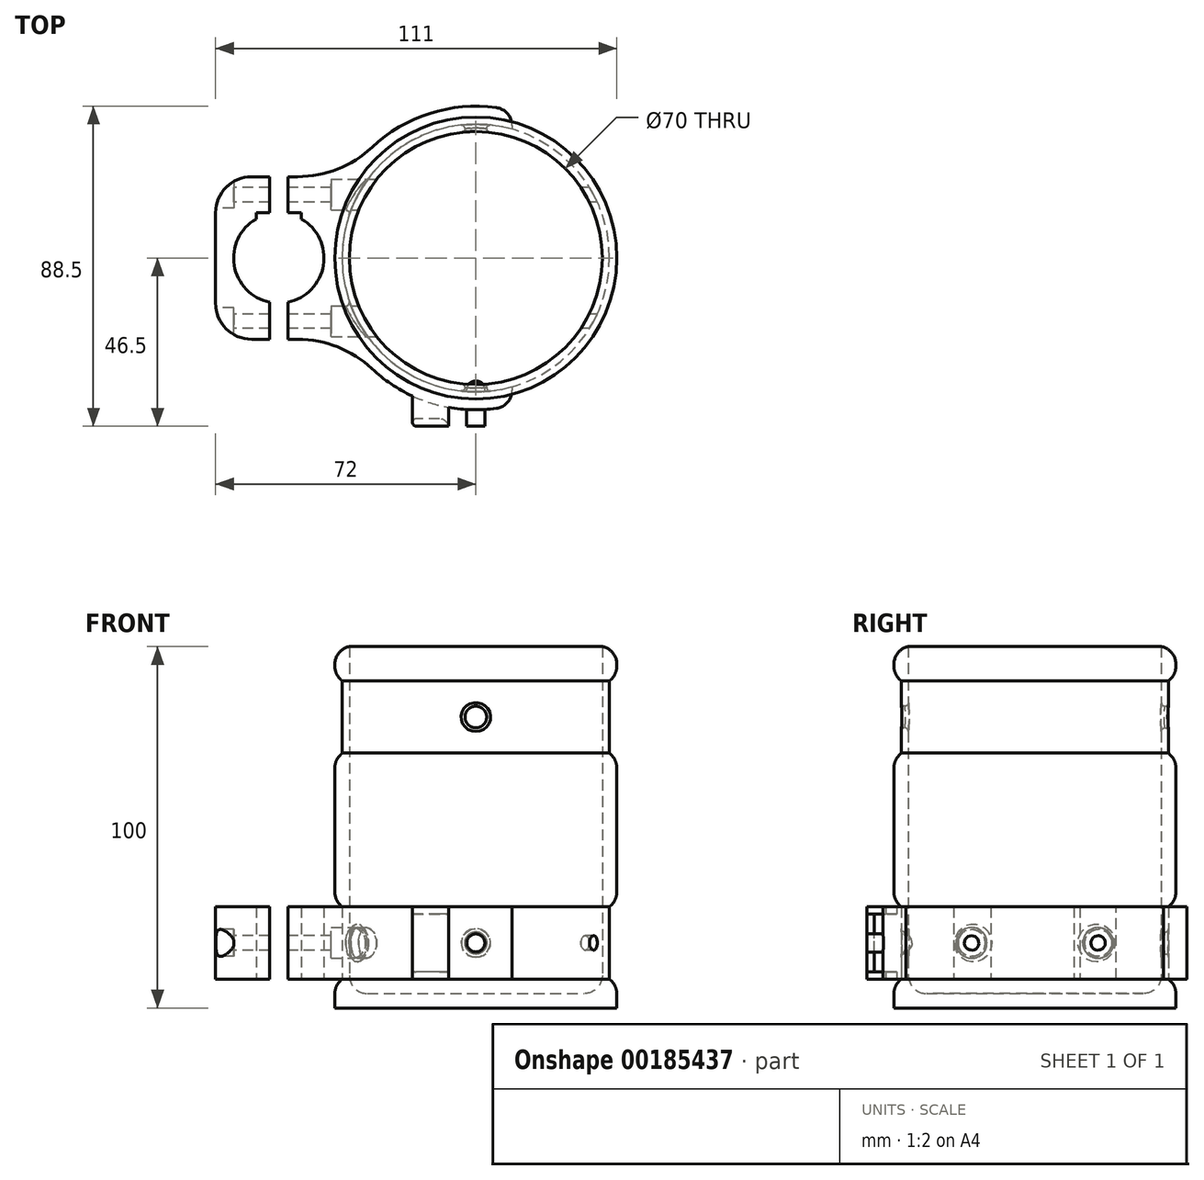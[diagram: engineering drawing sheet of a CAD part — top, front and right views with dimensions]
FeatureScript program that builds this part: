
annotation { "Feature Type Name" : "Feature", "Feature Type Description" : "" }
export const myFeature = defineFeature(function(context is Context, id is Id, definition is map)
    precondition{}
    {
        {
            var Q0;
            Q0=qCreatedBy(makeId("Front.planeOp"),FACE);
            var sketch = newSketch(context, id + "F0", { "sketchPlane" : qUnion([Q0])});
            skLineSegment(sketch, "E0", {"start": v(0, 0) * mm, "end": v(35, 0) * mm});
            skLineSegment(sketch, "E1", {"start": v(35, 0) * mm, "end": v(35, 100) * mm});
            skLineSegment(sketch, "E2", {"start": v(35, 100) * mm, "end": v(39, 100) * mm});
            skLineSegment(sketch, "E3", {"start": v(39, 100) * mm, "end": v(39, 92.5) * mm});
            skLineSegment(sketch, "E4", {"start": v(39, 92.5) * mm, "end": v(37, 90.5) * mm});
            skLineSegment(sketch, "E5", {"start": v(37, 90.5) * mm, "end": v(37, 70.5) * mm});
            skLineSegment(sketch, "E6", {"start": v(37, 70.5) * mm, "end": v(39, 68.5) * mm});
            skLineSegment(sketch, "E7", {"start": v(39, 68.5) * mm, "end": v(39, 30) * mm});
            skLineSegment(sketch, "E8", {"start": v(39, 30) * mm, "end": v(37, 28) * mm});
            skLineSegment(sketch, "E9", {"start": v(37, 28) * mm, "end": v(37, 8) * mm});
            skLineSegment(sketch, "E10", {"start": v(37, 8) * mm, "end": v(39, 6) * mm});
            skLineSegment(sketch, "E11", {"start": v(39, 6) * mm, "end": v(39, 0) * mm});
            skLineSegment(sketch, "E12", {"start": v(39, 0) * mm, "end": v(35, 0) * mm});
            skLineSegment(sketch, "E13", {"start": v(37, 8) * mm, "end": v(37, 6) * mm, "construction": true});
            skLineSegment(sketch, "E14", {"start": v(37, 6) * mm, "end": v(39, 6) * mm, "construction": true});
            skLineSegment(sketch, "E15", {"start": v(39, 30) * mm, "end": v(37, 30) * mm, "construction": true});
            skLineSegment(sketch, "E16", {"start": v(37, 30) * mm, "end": v(37, 28) * mm, "construction": true});
            skLineSegment(sketch, "E17", {"start": v(37, 70.5) * mm, "end": v(37, 68.5) * mm, "construction": true});
            skLineSegment(sketch, "E18", {"start": v(37, 68.5) * mm, "end": v(39, 68.5) * mm, "construction": true});
            skLineSegment(sketch, "E19", {"start": v(39, 92.5) * mm, "end": v(37, 92.5) * mm, "construction": true});
            skLineSegment(sketch, "E20", {"start": v(37, 92.5) * mm, "end": v(37, 90.5) * mm, "construction": true});
            skLineSegment(sketch, "E21", {"start": v(37, 6) * mm, "end": v(35, 6) * mm, "construction": true});
            skLineSegment(sketch, "E22", {"start": v(0, 0) * mm, "end": v(0, 100) * mm, "construction": true});
            skLineSegment(sketch, "E23", {"start": v(0, 100) * mm, "end": v(35, 100) * mm, "construction": true});
            skLineSegment(sketch, "E24", {"start": v(0, 4) * mm, "end": v(35, 4) * mm});
            skLineSegment(sketch, "E25", {"start": v(0, 4) * mm, "end": v(0, 0) * mm});
            skSolve(sketch);
        }
        {
            var Q0;
            Q0 = qSketchRegion(id + "F0", true);
            var Q1;
            Q1=sQuery(id+"F0.wireOp",EDGE,"E22");
            revolve(context, id + "F1", {"surfaceOperationType" : NewSurfaceOperationType.NEW, "entities" : qUnion([Q0]), "axis" : qUnion([Q1]), "revolveType" : RevolveType.FULL});
        }
        {
            var Q0;
            Q0=qCreatedBy(makeId("Front.planeOp"),FACE);
            var sketch = newSketch(context, id + "F2", { "sketchPlane" : qUnion([Q0])});
            skPoint(sketch, "E26", {"position": v(0, 28) * mm});
            skPoint(sketch, "E27", {"position": v(0, 8) * mm});
            skPoint(sketch, "E28", {"position": v(0, 70.5) * mm});
            skPoint(sketch, "E29", {"position": v(0, 90.5) * mm});
            skLineSegment(sketch, "E30", {"start": v(0, 70.5) * mm, "end": v(0, 90.5) * mm, "construction": true});
            skLineSegment(sketch, "E31", {"start": v(0, 8) * mm, "end": v(0, 28) * mm, "construction": true});
            skPoint(sketch, "E32", {"position": v(0, 18) * mm});
            skPoint(sketch, "E33", {"position": v(0, 80.5) * mm});
            skCircle(sketch, "E34", {"center": v(0, 18) * mm, "radius": 3 * mm});
            skCircle(sketch, "E35", {"center": v(0, 80.5) * mm, "radius": 3 * mm});
            skSolve(sketch);
        }
        {
            var Q0;
            Q0 = qSketchRegion(id + "F2", true);
            extrude(context, id + "F3", {"entities" : qUnion([Q0]), "operationType" : NewBodyOperationType.REMOVE, "oppositeDirection" : true, "depth" : 80 * mm, "symmetric" : true});
        }
        {
            var Q0;
            Q0=makeQuery(id+"F3.boolean.opBoolean","INTERSECT",EDGE,{"disambiguationData":[OD(0.0)],"derivedFrom":[makeQuery(id+"F1.opRevolve","SWEPT_FACE",FACE,{"disambiguationData":[OSD([sQuery(id+"F0.wireOp",EDGE,"E1")])]}),makeQuery(id+"F3.opExtrude","SWEPT_FACE",FACE,{"disambiguationData":[OSD([sQuery(id+"F2.wireOp",EDGE,"E35")])]})]});
            var Q1;
            Q1=makeQuery(id+"F3.boolean.opBoolean","INTERSECT",EDGE,{"disambiguationData":[OD(0.0)],"derivedFrom":[makeQuery(id+"F1.opRevolve","SWEPT_FACE",FACE,{"disambiguationData":[OSD([sQuery(id+"F0.wireOp",EDGE,"E5")])]}),makeQuery(id+"F3.opExtrude","SWEPT_FACE",FACE,{"disambiguationData":[OSD([sQuery(id+"F2.wireOp",EDGE,"E35")])]})]});
            var Q2;
            Q2=makeQuery(id+"F3.boolean.opBoolean","INTERSECT",EDGE,{"disambiguationData":[OD(0.0)],"derivedFrom":[makeQuery(id+"F1.opRevolve","SWEPT_FACE",FACE,{"disambiguationData":[OSD([sQuery(id+"F0.wireOp",EDGE,"E1")])]}),makeQuery(id+"F3.opExtrude","SWEPT_FACE",FACE,{"disambiguationData":[OSD([sQuery(id+"F2.wireOp",EDGE,"E34")])]})]});
            var Q3;
            Q3=makeQuery(id+"F3.boolean.opBoolean","INTERSECT",EDGE,{"disambiguationData":[OD(0.0)],"derivedFrom":[makeQuery(id+"F1.opRevolve","SWEPT_FACE",FACE,{"disambiguationData":[OSD([sQuery(id+"F0.wireOp",EDGE,"E9")])]}),makeQuery(id+"F3.opExtrude","SWEPT_FACE",FACE,{"disambiguationData":[OSD([sQuery(id+"F2.wireOp",EDGE,"E34")])]})]});
            var Q4;
            Q4=makeQuery(id+"F3.boolean.opBoolean","INTERSECT",EDGE,{"disambiguationData":[OD(1.0)],"derivedFrom":[makeQuery(id+"F1.opRevolve","SWEPT_FACE",FACE,{"disambiguationData":[OSD([sQuery(id+"F0.wireOp",EDGE,"E1")])]}),makeQuery(id+"F3.opExtrude","SWEPT_FACE",FACE,{"disambiguationData":[OSD([sQuery(id+"F2.wireOp",EDGE,"E35")])]})]});
            var Q5;
            Q5=makeQuery(id+"F3.boolean.opBoolean","INTERSECT",EDGE,{"disambiguationData":[OD(1.0)],"derivedFrom":[makeQuery(id+"F1.opRevolve","SWEPT_FACE",FACE,{"disambiguationData":[OSD([sQuery(id+"F0.wireOp",EDGE,"E5")])]}),makeQuery(id+"F3.opExtrude","SWEPT_FACE",FACE,{"disambiguationData":[OSD([sQuery(id+"F2.wireOp",EDGE,"E35")])]})]});
            var Q6;
            Q6=makeQuery(id+"F3.boolean.opBoolean","INTERSECT",EDGE,{"disambiguationData":[OD(1.0)],"derivedFrom":[makeQuery(id+"F1.opRevolve","SWEPT_FACE",FACE,{"disambiguationData":[OSD([sQuery(id+"F0.wireOp",EDGE,"E1")])]}),makeQuery(id+"F3.opExtrude","SWEPT_FACE",FACE,{"disambiguationData":[OSD([sQuery(id+"F2.wireOp",EDGE,"E34")])]})]});
            var Q7;
            Q7=makeQuery(id+"F3.boolean.opBoolean","INTERSECT",EDGE,{"disambiguationData":[OD(1.0)],"derivedFrom":[makeQuery(id+"F1.opRevolve","SWEPT_FACE",FACE,{"disambiguationData":[OSD([sQuery(id+"F0.wireOp",EDGE,"E9")])]}),makeQuery(id+"F3.opExtrude","SWEPT_FACE",FACE,{"disambiguationData":[OSD([sQuery(id+"F2.wireOp",EDGE,"E34")])]})]});
            fillet(context, id + "F4", {"entities" : qUnion([Q0, Q1, Q2, Q3, Q4, Q5, Q6, Q7]), "radius" : 1 * mm, "tangentPropagation" : true, "allowEdgeOverflow" : false});
        }
        {
            var Q0;
            Q0=makeQuery(id+"F1.opRevolve","SWEPT_EDGE",EDGE,{"disambiguationData":[OSD([sQuery(id+"F0.wireOp",EDGE,"E7"),sQuery(id+"F0.wireOp",EDGE,"E8")])]});
            var Q1;
            Q1=makeQuery(id+"F1.opRevolve","SWEPT_EDGE",EDGE,{"disambiguationData":[OSD([sQuery(id+"F0.wireOp",EDGE,"E10"),sQuery(id+"F0.wireOp",EDGE,"E11")])]});
            var Q2;
            Q2=makeQuery(id+"F1.opRevolve","SWEPT_EDGE",EDGE,{"disambiguationData":[OSD([sQuery(id+"F0.wireOp",EDGE,"E6"),sQuery(id+"F0.wireOp",EDGE,"E7")])]});
            var Q3;
            Q3=makeQuery(id+"F1.opRevolve","SWEPT_EDGE",EDGE,{"disambiguationData":[OSD([sQuery(id+"F0.wireOp",EDGE,"E3"),sQuery(id+"F0.wireOp",EDGE,"E4")])]});
            var Q4;
            Q4=makeQuery(id+"F1.opRevolve","SWEPT_EDGE",EDGE,{"disambiguationData":[OSD([sQuery(id+"F0.wireOp",EDGE,"E2"),sQuery(id+"F0.wireOp",EDGE,"E3")])]});
            fillet(context, id + "F5", {"entities" : qUnion([Q0, Q1, Q2, Q3, Q4]), "radius" : 5 * mm, "tangentPropagation" : true, "allowEdgeOverflow" : false});
        }
        {
            var Q0;
            Q0=makeQuery(id+"F1.opRevolve","SWEPT_EDGE",EDGE,{"disambiguationData":[OSD([sQuery(id+"F0.wireOp",EDGE,"E1"),sQuery(id+"F0.wireOp",EDGE,"E2")])]});
            var Q1;
            Q1=makeQuery(id+"F1.opRevolve","SWEPT_EDGE",EDGE,{"disambiguationData":[OSD([sQuery(id+"F0.wireOp",EDGE,"E1"),sQuery(id+"F0.wireOp",EDGE,"E24")])]});
            fillet(context, id + "F6", {"entities" : qUnion([Q0, Q1]), "radius" : 5 * mm, "tangentPropagation" : true, "allowEdgeOverflow" : false});
        }
        {
            var Q0;
            Q0=qCreatedBy(makeId("Top.planeOp"),FACE);
            var Q1;
            Q1=sQuery(id+"F2.wireOp",VERTEX,"E32");
            cPlane(context, id + "F7", {"entities" : qUnion([Q0, Q1]), "cplaneType" : CPlaneType.PLANE_POINT, "offset" : 25 * mm, "width" : 150 * mm, "height" : 150 * mm});
        }
        {
            var Q0;
            Q0=qCreatedBy(id+"F7.planeOp",FACE);
            var sketch = newSketch(context, id + "F8", { "sketchPlane" : qUnion([Q0])});
            skLineSegment(sketch, "E36", {"start": v(2.5, 0) * mm, "end": v(-2.5, 0) * mm, "construction": true});
            skLineSegment(sketch, "E37", {"start": v(-2.5, 0) * mm, "end": v(-2.5, 37) * mm, "construction": true});
            skLineSegment(sketch, "E38", {"start": v(-2.5, 37) * mm, "end": v(2.5, 37) * mm, "construction": true});
            skLineSegment(sketch, "E39", {"start": v(2.5, 37) * mm, "end": v(2.5, 0) * mm, "construction": true});
            skLineSegment(sketch, "E40", {"start": v(-2.5, 0) * mm, "end": v(-2.5, -37) * mm, "construction": true});
            skLineSegment(sketch, "E41", {"start": v(-2.5, -37) * mm, "end": v(2.5, -37) * mm, "construction": true});
            skLineSegment(sketch, "E42", {"start": v(2.5, -37) * mm, "end": v(2.5, 0) * mm, "construction": true});
            skLineSegment(sketch, "E43", {"start": v(0, 0) * mm, "end": v(-42, 0) * mm, "construction": true});
            skArc(sketch, "E44", {"start": v(-60.75, 10.83) * mm, "mid": v(-54.5, -12.5) * mm, "end": v(-48.25, 10.83) * mm});
            skLineSegment(sketch, "E45", {"start": v(-54.5, 0) * mm, "end": v(-42, 0) * mm, "construction": true});
            skPoint(sketch, "E46", {"position": v(-48.25, 0) * mm});
            skLineSegment(sketch, "E47", {"start": v(-48.25, 10.83) * mm, "end": v(-48.25, -10.83) * mm, "construction": true});
            skArc(sketch, "E48", {"start": v(10, 35.62) * mm, "mid": v(-37, 0) * mm, "end": v(10, -35.62) * mm});
            skPoint(sketch, "E49", {"position": v(0, -37) * mm});
            skLineSegment(sketch, "E50", {"start": v(0, -37) * mm, "end": v(10, -37) * mm, "construction": true});
            skPoint(sketch, "E51", {"position": v(0, 37) * mm});
            skLineSegment(sketch, "E52", {"start": v(0, 37) * mm, "end": v(10, 37) * mm, "construction": true});
            skLineSegment(sketch, "E53", {"start": v(10, 37) * mm, "end": v(10, -37) * mm, "construction": true});
            skPoint(sketch, "E54", {"position": v(10, -35.62) * mm});
            skPoint(sketch, "E55", {"position": v(10, 35.62) * mm});
            skArc(sketch, "E56", {"start": v(10, 40.8) * mm, "mid": v(-42, 0) * mm, "end": v(10, -40.8) * mm});
            skLineSegment(sketch, "E57", {"start": v(10, -35.62) * mm, "end": v(10, -40.8) * mm});
            skLineSegment(sketch, "E58", {"start": v(10, 40.8) * mm, "end": v(10, 35.62) * mm});
            skLineSegment(sketch, "E59", {"start": v(-42, -15) * mm, "end": v(-42, 0) * mm, "construction": true});
            skLineSegment(sketch, "E60", {"start": v(-42, 15) * mm, "end": v(-42, 0) * mm, "construction": true});
            skLineSegment(sketch, "E61", {"start": v(-48.25, 12.5) * mm, "end": v(-60.75, 12.5) * mm});
            skLineSegment(sketch, "E62", {"start": v(-48.25, 12.5) * mm, "end": v(-48.25, 10.83) * mm});
            skLineSegment(sketch, "E63", {"start": v(-60.75, 12.5) * mm, "end": v(-60.75, 10.83) * mm});
            skLineSegment(sketch, "E64", {"start": v(-54.5, 12.5) * mm, "end": v(-54.5, -12.5) * mm, "construction": true});
            skPoint(sketch, "E65", {"position": v(-54.5, 12.5) * mm});
            skPoint(sketch, "E66", {"position": v(-54.5, -12.5) * mm});
            skLineSegment(sketch, "E67", {"start": v(-52, 22.5) * mm, "end": v(-52, -22.5) * mm});
            skLineSegment(sketch, "E68", {"start": v(-57, 22.5) * mm, "end": v(-57, -22.5) * mm});
            skLineSegment(sketch, "E69", {"start": v(-52, 12.5) * mm, "end": v(-57, 12.5) * mm, "construction": true});
            skLineSegment(sketch, "E70", {"start": v(-54.5, 12.5) * mm, "end": v(-54.5, 15.5) * mm, "construction": true});
            skPoint(sketch, "E71", {"position": v(-54.5, 17.5) * mm});
            skLineSegment(sketch, "E72", {"start": v(-54.5, 19.5) * mm, "end": v(-54.5, 15.5) * mm, "construction": true});
            skLineSegment(sketch, "E73.trimOffspring", {"start": v(-54.5, 19.5) * mm, "end": v(-54.5, 22.5) * mm, "construction": true});
            skLineSegment(sketch, "E74", {"start": v(-35.46, 22.5) * mm, "end": v(-72, 22.5) * mm});
            skLineSegment(sketch, "E75", {"start": v(-67, 22.5) * mm, "end": v(-67, 19.5) * mm, "construction": true});
            skLineSegment(sketch, "E76", {"start": v(-72, -22.5) * mm, "end": v(-35.46, -22.5) * mm});
            skLineSegment(sketch, "E77", {"start": v(-72, 22.5) * mm, "end": v(-72, -22.5) * mm});
            skLineSegment(sketch, "E78", {"start": v(-31.44, 19.5) * mm, "end": v(-72, 19.5) * mm, "construction": true});
            skLineSegment(sketch, "E79", {"start": v(-33.6, 15.5) * mm, "end": v(-72, 15.5) * mm, "construction": true});
            skLineSegment(sketch, "E80", {"start": v(-72, -15.5) * mm, "end": v(-33.6, -15.5) * mm, "construction": true});
            skLineSegment(sketch, "E81", {"start": v(-72, -19.5) * mm, "end": v(-31.44, -19.5) * mm, "construction": true});
            skLineSegment(sketch, "E82", {"start": v(-67, 19.5) * mm, "end": v(-67, 15.5) * mm, "construction": true});
            skLineSegment(sketch, "E83", {"start": v(-67, 15.5) * mm, "end": v(-67, -15.5) * mm, "construction": true});
            skLineSegment(sketch, "E84", {"start": v(-67, -15.5) * mm, "end": v(-67, -19.5) * mm, "construction": true});
            skLineSegment(sketch, "E85", {"start": v(-67, -19.5) * mm, "end": v(-67, -22.5) * mm, "construction": true});
            skLineSegment(sketch, "E86", {"start": v(-72, 17.5) * mm, "end": v(-32.6, 17.5) * mm, "construction": true});
            skLineSegment(sketch, "E87", {"start": v(-72, -17.5) * mm, "end": v(-32.6, -17.5) * mm, "construction": true});
            skSolve(sketch);
        }
        {
            var Q0;
            Q0=makeQuery(id+"F8.imprint","IMPRINT",FACE,{"disambiguationData":[TD([[makeQuery(id+"F8.imprint","IMPRINT",EDGE,{"derivedFrom":sQuery(id+"F8.wireOp",EDGE,"E48")}),-1.0]])]});
            var Q1;
            {var subQ0=sQuery(id+"F8.wireOp",EDGE,"E67");var subQ1=sQuery(id+"F8.wireOp",EDGE,"E44");var subQ2=makeQuery(id+"F8.imprint","INTERSECT",VERTEX,{"derivedFrom":[subQ1,subQ0]});Q1=makeQuery(id+"F8.imprint","IMPRINT",FACE,{"disambiguationData":[TD([[makeQuery(id+"F8.imprint","IMPRINT",EDGE,{"disambiguationData":[TD([[subQ2,-1.0]])],"derivedFrom":subQ1}),-1.0]])]});}
            var Q2;
            {var subQ0=sQuery(id+"F8.wireOp",EDGE,"E62");Q2=makeQuery(id+"F8.imprint","IMPRINT",FACE,{"disambiguationData":[TD([[makeQuery(id+"F8.imprint","IMPRINT",EDGE,{"derivedFrom":subQ0}),1.0]])]});}
            extrude(context, id + "F9", {"entities" : qUnion([Q0, Q1, Q2]), "depth" : 20 * mm, "symmetric" : true});
        }
        {
            var Q0;
            {var subQ5=sQuery(id+"F8.wireOp",EDGE,"E63");Q0=makeQuery(id+"F8.imprint","IMPRINT",FACE,{"disambiguationData":[TD([[makeQuery(id+"F8.imprint","IMPRINT",EDGE,{"derivedFrom":subQ5}),-1.0]])]});}
            extrude(context, id + "F10", {"entities" : qUnion([Q0]), "depth" : 20 * mm, "symmetric" : true});
        }
        {
            var Q0;
            Q0=makeQuery(id+"F9.opExtrude","SWEPT_EDGE",EDGE,{"disambiguationData":[OSD([sQuery(id+"F8.wireOp",EDGE,"E56"),sQuery(id+"F8.wireOp",EDGE,"E76")])]});
            var Q1;
            Q1=makeQuery(id+"F9.opExtrude","SWEPT_EDGE",EDGE,{"disambiguationData":[OSD([sQuery(id+"F8.wireOp",EDGE,"E56"),sQuery(id+"F8.wireOp",EDGE,"E74")])]});
            fillet(context, id + "F11", {"entities" : qUnion([Q0, Q1]), "radius" : 30 * mm, "tangentPropagation" : true, "allowEdgeOverflow" : false});
        }
        {
            var Q0;
            Q0=makeQuery(id+"F10.opExtrude","SWEPT_FACE",FACE,{"disambiguationData":[OSD([sQuery(id+"F8.wireOp",EDGE,"E77")])]});
            var sketch = newSketch(context, id + "F12", { "sketchPlane" : qUnion([Q0])});
            skPoint(sketch, "E88", {"position": v(17.5, 18) * mm});
            skPoint(sketch, "E89", {"position": v(19.5, 18) * mm});
            skPoint(sketch, "E90", {"position": v(15.5, 18) * mm});
            skCircle(sketch, "E91", {"center": v(17.5, 18) * mm, "radius": 2 * mm});
            skPoint(sketch, "E92", {"position": v(-19.5, 18) * mm});
            skPoint(sketch, "E93", {"position": v(-17.5, 18) * mm});
            skPoint(sketch, "E94", {"position": v(-15.5, 18) * mm});
            skCircle(sketch, "E95", {"center": v(-17.5, 18) * mm, "radius": 2 * mm});
            skCircle(sketch, "E96", {"center": v(-17.5, 18) * mm, "radius": 3.75 * mm});
            skCircle(sketch, "E97", {"center": v(17.5, 18) * mm, "radius": 3.75 * mm});
            skSolve(sketch);
        }
        {
            var Q0;
            Q0=makeQuery(id+"F12.imprint","IMPRINT",FACE,{"disambiguationData":[TD([[makeQuery(id+"F12.imprint","IMPRINT",EDGE,{"derivedFrom":sQuery(id+"F12.wireOp",EDGE,"E95")}),1.0]])]});
            var Q1;
            Q1=makeQuery(id+"F12.imprint","IMPRINT",FACE,{"disambiguationData":[TD([[makeQuery(id+"F12.imprint","IMPRINT",EDGE,{"derivedFrom":sQuery(id+"F12.wireOp",EDGE,"E91")}),1.0]])]});
            extrude(context, id + "F13", {"entities" : qUnion([Q0, Q1]), "operationType" : NewBodyOperationType.REMOVE, "endBound" : BoundingType.THROUGH_ALL, "oppositeDirection" : true, "depth" : 25 * mm});
        }
        {
            var Q0;
            Q0=makeQuery(id+"F12.imprint","IMPRINT",FACE,{"disambiguationData":[TD([[makeQuery(id+"F12.imprint","IMPRINT",EDGE,{"derivedFrom":sQuery(id+"F12.wireOp",EDGE,"E95")}),-1.0]])]});
            var Q1;
            Q1=makeQuery(id+"F12.imprint","IMPRINT",FACE,{"disambiguationData":[TD([[makeQuery(id+"F12.imprint","IMPRINT",EDGE,{"derivedFrom":sQuery(id+"F12.wireOp",EDGE,"E91")}),-1.0]])]});
            extrude(context, id + "F14", {"entities" : qUnion([Q0, Q1]), "operationType" : NewBodyOperationType.REMOVE, "oppositeDirection" : true, "depth" : 5 * mm});
        }
        {
            var Q0;
            Q0=makeQuery(id+"F9.opExtrude","SWEPT_EDGE",EDGE,{"disambiguationData":[OSD([sQuery(id+"F8.wireOp",EDGE,"E56"),sQuery(id+"F8.wireOp",EDGE,"E57")])]});
            var Q1;
            Q1=makeQuery(id+"F9.opExtrude","SWEPT_EDGE",EDGE,{"disambiguationData":[OSD([sQuery(id+"F8.wireOp",EDGE,"E56"),sQuery(id+"F8.wireOp",EDGE,"E58")])]});
            fillet(context, id + "F15", {"entities" : qUnion([Q0, Q1]), "radius" : 5 * mm, "tangentPropagation" : true, "allowEdgeOverflow" : false});
        }
        {
            var Q0;
            Q0=qCreatedBy(makeId("Right.planeOp"),FACE);
            var sketch = newSketch(context, id + "F16", { "sketchPlane" : qUnion([Q0])});
            skPoint(sketch, "E98", {"position": v(-17.5, 18) * mm});
            skPoint(sketch, "E99", {"position": v(17.5, 18) * mm});
            skCircle(sketch, "E100", {"center": v(-17.5, 18) * mm, "radius": 4.25 * mm});
            skCircle(sketch, "E101", {"center": v(17.5, 18) * mm, "radius": 4.25 * mm});
            skSolve(sketch);
        }
        {
            var Q0;
            Q0 = qSketchRegion(id + "F16", true);
            extrude(context, id + "F17", {"entities" : qUnion([Q0]), "operationType" : NewBodyOperationType.REMOVE, "oppositeDirection" : true, "depth" : 40 * mm});
        }
        {
            var Q0;
            Q0=makeQuery(id+"F17.boolean.opBoolean","INTERSECT",EDGE,{"derivedFrom":[makeQuery(id+"F9.opExtrude","SWEPT_FACE",FACE,{"disambiguationData":[OSD([sQuery(id+"F8.wireOp",EDGE,"E48")])]}),makeQuery(id+"F17.opExtrude","SWEPT_FACE",FACE,{"disambiguationData":[OSD([sQuery(id+"F16.wireOp",EDGE,"E101")])]})]});
            var Q1;
            Q1=makeQuery(id+"F17.boolean.opBoolean","INTERSECT",EDGE,{"derivedFrom":[makeQuery(id+"F9.opExtrude","SWEPT_FACE",FACE,{"disambiguationData":[OSD([sQuery(id+"F8.wireOp",EDGE,"E48")])]}),makeQuery(id+"F17.opExtrude","SWEPT_FACE",FACE,{"disambiguationData":[OSD([sQuery(id+"F16.wireOp",EDGE,"E100")])]})]});
            fillet(context, id + "F18", {"entities" : qUnion([Q0, Q1]), "radius" : 1 * mm, "tangentPropagation" : true, "allowEdgeOverflow" : false});
        }
        {
            var Q0;
            Q0=qCreatedBy(makeId("Front.planeOp"),FACE);
            cPlane(context, id + "F19", {"entities" : qUnion([Q0]), "cplaneType" : CPlaneType.OFFSET, "offset" : 39 * mm, "width" : 150 * mm, "height" : 150 * mm});
        }
        {
            var Q0;
            Q0=qCreatedBy(id+"F19.planeOp",FACE);
            var sketch = newSketch(context, id + "F20", { "sketchPlane" : qUnion([Q0])});
            skPoint(sketch, "E102", {"position": v(0, 18) * mm});
            skCircle(sketch, "E103", {"center": v(0, 18) * mm, "radius": 2.5 * mm});
            skSolve(sketch);
        }
        {
            var Q0;
            Q0=makeQuery(id+"F20.imprint","IMPRINT",FACE,{"disambiguationData":[TD([[makeQuery(id+"F20.imprint","IMPRINT",EDGE,{"derivedFrom":sQuery(id+"F20.wireOp",EDGE,"E103")}),1.0]])]});
            extrude(context, id + "F21", {"entities" : qUnion([Q0]), "operationType" : NewBodyOperationType.ADD, "depth" : 7.5 * mm, "hasSecondDirection" : true, "secondDirectionOppositeDirection" : true, "secondDirectionDepth" : 5 * mm});
        }
        {
            var Q0;
            Q0=makeQuery(id+"F21.opExtrude","CAP_EDGE",EDGE,{"disambiguationData":[OSD([sQuery(id+"F20.wireOp",EDGE,"E103")])],"isStart":true});
            var Q1;
            Q1=makeQuery(id+"FAa4vTVfSFpXn4T_2.1.F21.opExtrude","CAP_EDGE",EDGE,{"disambiguationData":[OSD([sQuery(id+"F20.wireOp",EDGE,"E103")])],"isStart":true});
            fillet(context, id + "F22", {"entities" : qUnion([Q0, Q1]), "radius" : 2.5 * mm, "tangentPropagation" : true, "allowEdgeOverflow" : false});
        }
        {
            var Q0;
            Q0=qCreatedBy(makeId("Right.planeOp"),FACE);
            cPlane(context, id + "F23", {"entities" : qUnion([Q0]), "cplaneType" : CPlaneType.OFFSET, "offset" : 12.5 * mm, "oppositeDirection" : true, "width" : 150 * mm, "height" : 150 * mm});
        }
        {
            var Q0;
            Q0=qCreatedBy(id+"F23.planeOp",FACE);
            var sketch = newSketch(context, id + "F24", { "sketchPlane" : qUnion([Q0])});
            skPoint(sketch, "E104", {"position": v(-36.66, 28) * mm});
            skPoint(sketch, "E105", {"position": v(-46.5, 28) * mm});
            skPoint(sketch, "E106", {"position": v(-46.5, 8) * mm});
            skPoint(sketch, "E107", {"position": v(-36.66, 8) * mm});
            skLineSegment(sketch, "E108", {"start": v(-36.66, 28) * mm, "end": v(-46.5, 28) * mm});
            skLineSegment(sketch, "E109", {"start": v(-46.5, 8) * mm, "end": v(-36.66, 8) * mm});
            skLineSegment(sketch, "E110", {"start": v(-46.5, 8) * mm, "end": v(-46.5, 28) * mm});
            skLineSegment(sketch, "E111", {"start": v(-36.66, 8) * mm, "end": v(-36.66, 10) * mm});
            skLineSegment(sketch, "E112", {"start": v(-36.66, 10) * mm, "end": v(-44.5, 10) * mm});
            skLineSegment(sketch, "E113", {"start": v(-44.5, 10) * mm, "end": v(-44.5, 26) * mm});
            skLineSegment(sketch, "E114", {"start": v(-44.5, 26) * mm, "end": v(-36.66, 26) * mm});
            skLineSegment(sketch, "E115", {"start": v(-36.66, 26) * mm, "end": v(-36.66, 28) * mm});
            skLineSegment(sketch, "E116", {"start": v(-44.5, 26) * mm, "end": v(-46.5, 26) * mm, "construction": true});
            skSolve(sketch);
        }
        {
            var Q0;
            Q0 = qSketchRegion(id + "F24", true);
            extrude(context, id + "F25", {"entities" : qUnion([Q0]), "operationType" : NewBodyOperationType.ADD, "depth" : 10 * mm, "symmetric" : true});
        }
        {
            var Q0;
            Q0=makeQuery(id+"F25.opExtrude","CAP_EDGE",EDGE,{"disambiguationData":[OSD([sQuery(id+"F24.wireOp",EDGE,"E113")])],"isStart":false});
            fillet(context, id + "F26", {"entities" : qUnion([Q0]), "radius" : 2.5 * mm, "tangentPropagation" : true, "allowEdgeOverflow" : false});
        }
        {
            var Q0;
            Q0=makeQuery(id+"F25.opExtrude","CAP_EDGE",EDGE,{"disambiguationData":[OSD([sQuery(id+"F24.wireOp",EDGE,"E113")])],"isStart":true});
            var Q1;
            Q1=makeQuery(id+"F25.opExtrude","CAP_EDGE",EDGE,{"disambiguationData":[OSD([sQuery(id+"F24.wireOp",EDGE,"E110")])],"isStart":true});
            fillet(context, id + "F27", {"entities" : qUnion([Q0, Q1]), "radius" : 1 * mm, "tangentPropagation" : true, "allowEdgeOverflow" : false});
        }
        {
            var Q0;
            Q0=makeQuery(id+"F10.opExtrude","SWEPT_EDGE",EDGE,{"disambiguationData":[OSD([sQuery(id+"F8.wireOp",EDGE,"E76"),sQuery(id+"F8.wireOp",EDGE,"E77")])]});
            var Q1;
            Q1=makeQuery(id+"F10.opExtrude","SWEPT_EDGE",EDGE,{"disambiguationData":[OSD([sQuery(id+"F8.wireOp",EDGE,"E74"),sQuery(id+"F8.wireOp",EDGE,"E77")])]});
            fillet(context, id + "F28", {"entities" : qUnion([Q0, Q1]), "radius" : 10 * mm, "tangentPropagation" : true, "allowEdgeOverflow" : false});
        }
    });
